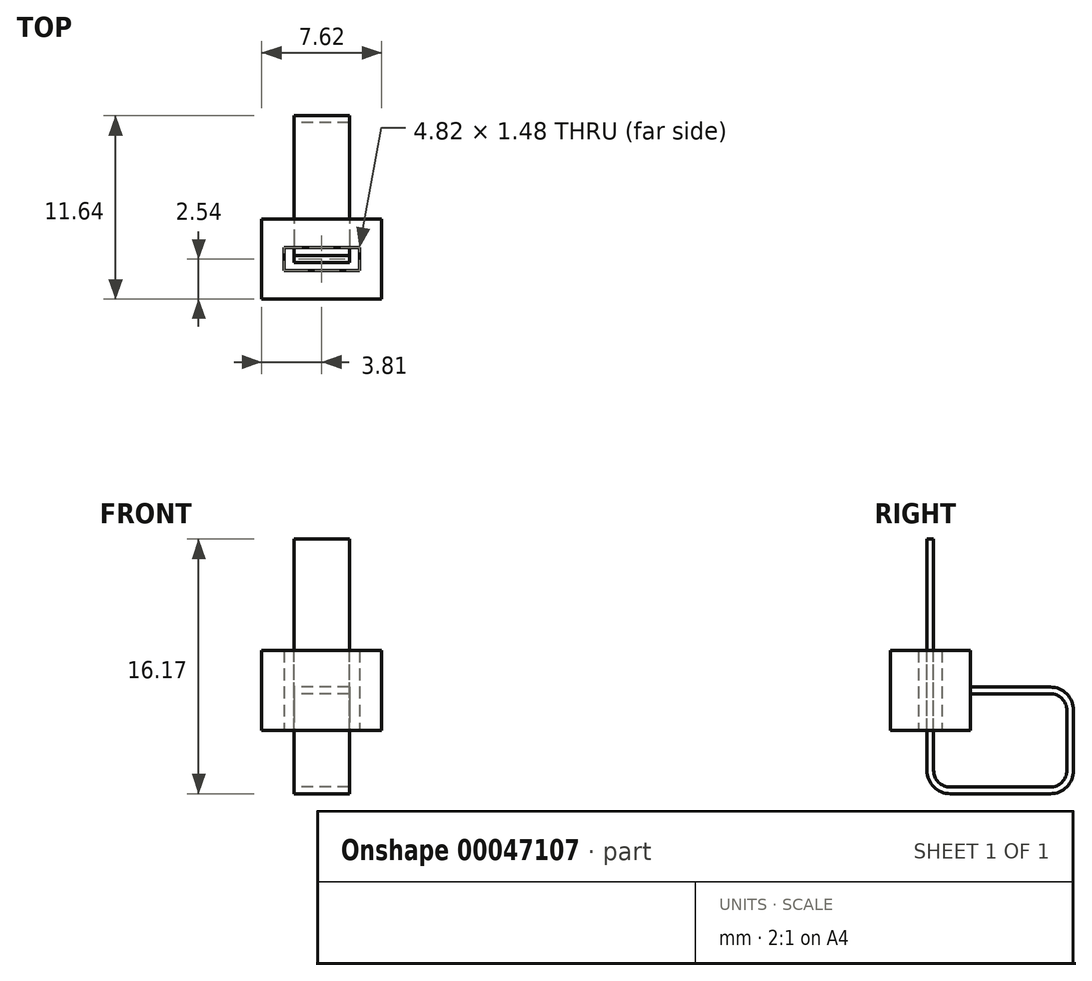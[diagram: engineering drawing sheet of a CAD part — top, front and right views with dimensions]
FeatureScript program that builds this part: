
annotation { "Feature Type Name" : "Feature", "Feature Type Description" : "" }
export const myFeature = defineFeature(function(context is Context, id is Id, definition is map)
    precondition{}
    {
        {
            var Q0;
            Q0=qCreatedBy(makeId("Right.planeOp"),FACE);
            var sketch = newSketch(context, id + "F0", { "sketchPlane" : qUnion([Q0])});
            skLineSegment(sketch, "E0.rect.bottom", {"start": v(2.54, 2.54) * mm, "end": v(-2.54, 2.54) * mm});
            skLineSegment(sketch, "E0.rect.top", {"start": v(2.54, -2.54) * mm, "end": v(-2.54, -2.54) * mm});
            skLineSegment(sketch, "E0.rect.left", {"start": v(2.54, 2.54) * mm, "end": v(2.54, -2.54) * mm});
            skLineSegment(sketch, "E0.rect.right", {"start": v(-2.54, 2.54) * mm, "end": v(-2.54, -2.54) * mm});
            skPoint(sketch, "E0.rect.middle", {"position": v(0, 0) * mm});
            skSolve(sketch);
        }
        {
            var Q0;
            Q0=qSketchRegion(id+"F0",true);
            extrude(context, id + "F1", {"entities" : qUnion([Q0]), "endBound" : BoundingType.SYMMETRIC, "depth" : 7.62 * mm});
        }
        {
            var Q0;
            Q0=qCreatedBy(makeId("Right.planeOp"),FACE);
            var sketch = newSketch(context, id + "F2", { "sketchPlane" : qUnion([Q0])});
            skLineSegment(sketch, "E1", {"start": v(2.54, 0) * mm, "end": v(7.62, 0) * mm});
            skLineSegment(sketch, "E2", {"start": v(8.9, -1.27) * mm, "end": v(8.9, -5.08) * mm});
            skLineSegment(sketch, "E3", {"start": v(7.62, -6.35) * mm, "end": v(1.27, -6.35) * mm});
            skLineSegment(sketch, "E4", {"start": v(0, -5.08) * mm, "end": v(0, 9.6) * mm});
            skPoint(sketch, "E5.visualSharp", {"position": v(8.9, 0) * mm});
            skArc(sketch, "E5.filletArc", {"start": v(8.9, -1.27) * mm, "mid": v(8.52, -0.37) * mm, "end": v(7.62, 0) * mm});
            skPoint(sketch, "E6.visualSharp", {"position": v(8.9, -6.35) * mm});
            skArc(sketch, "E6.filletArc", {"start": v(7.62, -6.35) * mm, "mid": v(8.52, -5.98) * mm, "end": v(8.9, -5.08) * mm});
            skPoint(sketch, "E7.visualSharp", {"position": v(0, -6.35) * mm});
            skArc(sketch, "E7.filletArc", {"start": v(0, -5.08) * mm, "mid": v(0.37, -5.98) * mm, "end": v(1.27, -6.35) * mm});
            skPoint(sketch, "E8.orphan", {"position": v(0, 0) * mm});
            skPoint(sketch, "E9.orphan", {"position": v(2.54, 2.54) * mm});
            skPoint(sketch, "E10.0.end.orphan", {"position": v(2.54, -2.54) * mm});
            skSolve(sketch);
        }
        {
            var Q0;
            Q0=makeQuery(id+"F1.opExtrude","SWEPT_FACE",FACE,{"disambiguationData":[OSD([sQuery(id+"F0.wireOp",EDGE,"E0.rect.left")])]});
            var sketch = newSketch(context, id + "F3", { "sketchPlane" : qUnion([Q0])});
            skLineSegment(sketch, "E11.rect.bottom", {"start": v(-1.75, 0.21) * mm, "end": v(1.75, 0.21) * mm});
            skLineSegment(sketch, "E11.rect.top", {"start": v(-1.75, -0.21) * mm, "end": v(1.75, -0.21) * mm});
            skLineSegment(sketch, "E11.rect.left", {"start": v(-1.75, 0.21) * mm, "end": v(-1.75, -0.21) * mm});
            skLineSegment(sketch, "E11.rect.right", {"start": v(1.75, 0.21) * mm, "end": v(1.75, -0.21) * mm});
            skPoint(sketch, "E11.rect.middle", {"position": v(0, 0) * mm});
            skSolve(sketch);
        }
        {
            var Q0;
            Q0=makeQuery(id+"F3.imprint","IMPRINT",FACE,{"disambiguationData":[TD([[makeQuery(id+"F3.imprint","IMPRINT",EDGE,{"derivedFrom":sQuery(id+"F3.wireOp",EDGE,"E11.rect.bottom")}),-1.0]])]});
            var Q1;
            Q1=sQuery(id+"F2.wireOp",EDGE,"E1");
            var Q2;
            Q2=sQuery(id+"F2.wireOp",EDGE,"E5.filletArc");
            var Q3;
            Q3=sQuery(id+"F2.wireOp",EDGE,"E2");
            var Q4;
            Q4=sQuery(id+"F2.wireOp",EDGE,"E6.filletArc");
            var Q5;
            Q5=sQuery(id+"F2.wireOp",EDGE,"E3");
            var Q6;
            Q6=sQuery(id+"F2.wireOp",EDGE,"E7.filletArc");
            var Q7;
            Q7=sQuery(id+"F2.wireOp",EDGE,"E4");
            sweep(context, id + "F4", {"operationType" : NewBodyOperationType.ADD, "profiles" : qUnion([Q0]), "path" : qUnion([Q1, Q2, Q3, Q4, Q5, Q6, Q7])});
        }
        {
            var Q0;
            Q0=makeQuery(id+"F1.opExtrude","SWEPT_FACE",FACE,{"disambiguationData":[OSD([sQuery(id+"F0.wireOp",EDGE,"E0.rect.top")])]});
            var sketch = newSketch(context, id + "F5", { "sketchPlane" : qUnion([Q0])});
            skLineSegment(sketch, "E12.rect.bottom", {"start": v(2.4, 0.74) * mm, "end": v(-2.4, 0.74) * mm});
            skLineSegment(sketch, "E12.rect.top", {"start": v(2.4, -0.74) * mm, "end": v(-2.4, -0.74) * mm});
            skLineSegment(sketch, "E12.rect.left", {"start": v(2.4, 0.74) * mm, "end": v(2.4, -0.74) * mm});
            skLineSegment(sketch, "E12.rect.right", {"start": v(-2.4, 0.74) * mm, "end": v(-2.4, -0.74) * mm});
            skPoint(sketch, "E12.rect.middle", {"position": v(0, 0) * mm});
            skSolve(sketch);
        }
        {
            var Q0;
            Q0=makeQuery(id+"F5.imprint","IMPRINT",FACE,{"disambiguationData":[TD([[makeQuery(id+"F5.imprint","IMPRINT",EDGE,{"derivedFrom":sQuery(id+"F5.wireOp",EDGE,"E12.rect.bottom")}),1.0]])]});
            extrude(context, id + "F6", {"entities" : qUnion([Q0]), "operationType" : NewBodyOperationType.REMOVE, "endBound" : BoundingType.UP_TO_NEXT, "oppositeDirection" : true, "depth" : 25.4 * mm});
        }
    });
